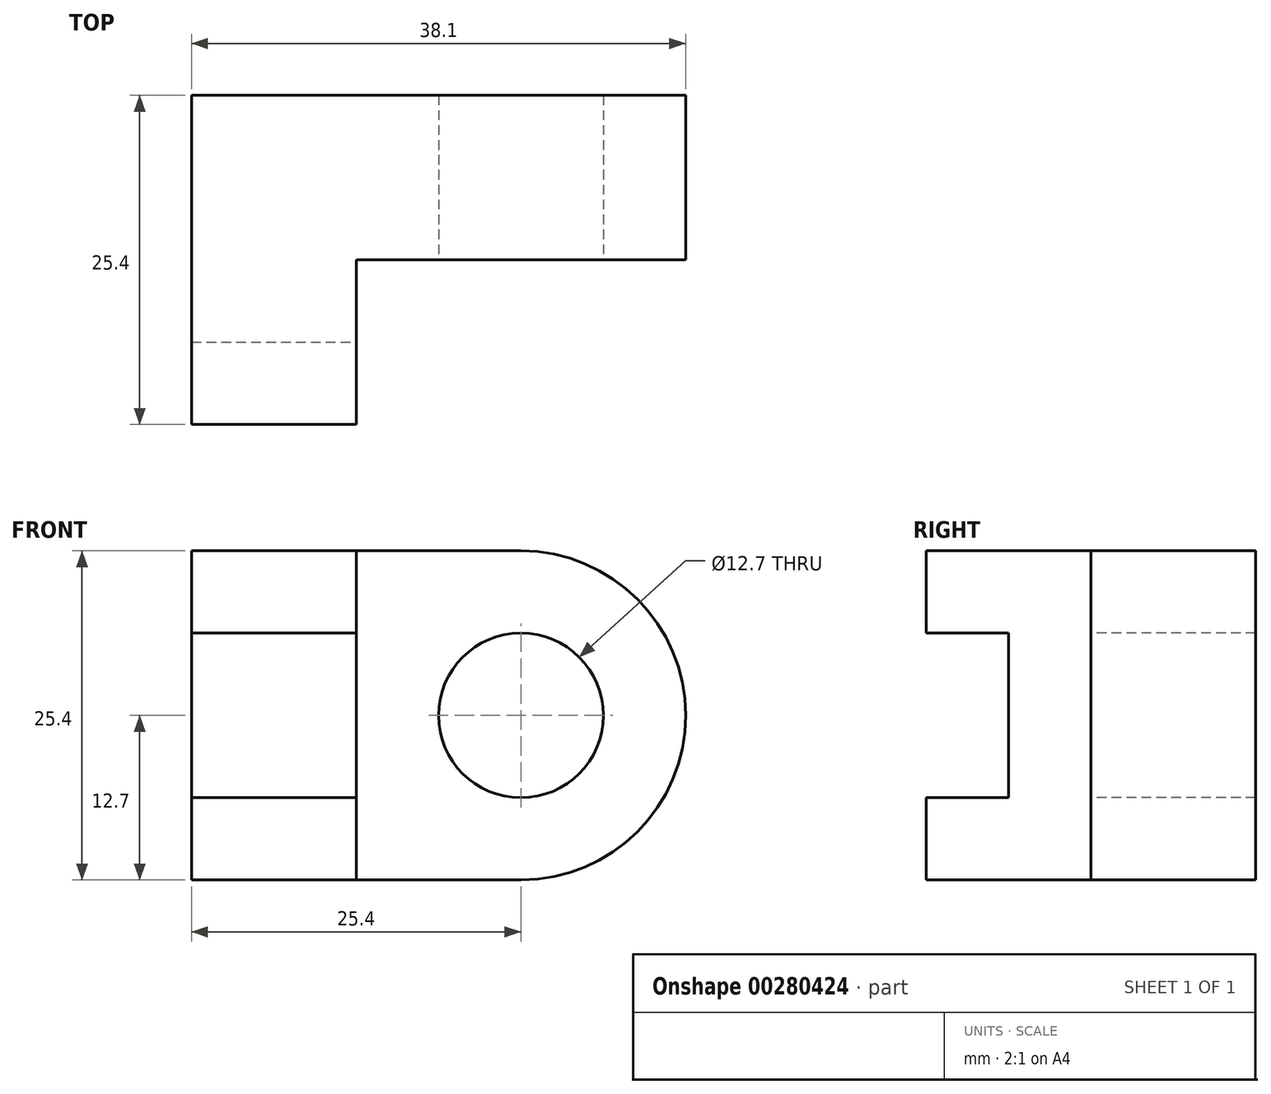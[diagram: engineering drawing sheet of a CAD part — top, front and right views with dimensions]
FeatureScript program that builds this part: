
annotation { "Feature Type Name" : "Feature", "Feature Type Description" : "" }
export const myFeature = defineFeature(function(context is Context, id is Id, definition is map)
    precondition{}
    {
        {
            var Q0;
            Q0=qCreatedBy(makeId("Front.planeOp"),FACE);
            var sketch = newSketch(context, id + "F0", { "sketchPlane" : qUnion([Q0])});
            skLineSegment(sketch, "E0", {"start": v(0, 0) * mm, "end": v(38.1, 0) * mm});
            skLineSegment(sketch, "E1", {"start": v(38.1, 0) * mm, "end": v(38.1, 25.4) * mm});
            skLineSegment(sketch, "E2", {"start": v(38.1, 25.4) * mm, "end": v(0, 25.4) * mm});
            skLineSegment(sketch, "E3", {"start": v(0, 25.4) * mm, "end": v(0, 0) * mm});
            skSolve(sketch);
        }
        {
            var Q0;
            Q0 = qSketchRegion(id + "F0", true);
            extrude(context, id + "F1", {"entities" : qUnion([Q0]), "depth" : 25.4 * mm, "symmetric" : true});
        }
        {
            var Q0;
            Q0=makeQuery(id+"F1.opExtrude","CAP_FACE",FACE,{"disambiguationData":[OSD([sQuery(id+"F0.wireOp",EDGE,"E0"),sQuery(id+"F0.wireOp",EDGE,"E1"),sQuery(id+"F0.wireOp",EDGE,"E2"),sQuery(id+"F0.wireOp",EDGE,"E3")])],"isStart":false});
            var sketch = newSketch(context, id + "F2", { "sketchPlane" : qUnion([Q0])});
            skLineSegment(sketch, "E4", {"start": v(0, 6.35) * mm, "end": v(12.7, 6.35) * mm});
            skLineSegment(sketch, "E5", {"start": v(12.7, 6.35) * mm, "end": v(12.7, 19.05) * mm});
            skLineSegment(sketch, "E6", {"start": v(12.7, 19.05) * mm, "end": v(0, 19.05) * mm});
            skLineSegment(sketch, "E7", {"start": v(0, 19.05) * mm, "end": v(0, 6.35) * mm});
            skSolve(sketch);
        }
        {
            var Q0;
            Q0 = qSketchRegion(id + "F2", true);
            extrude(context, id + "F3", {"entities" : qUnion([Q0]), "operationType" : NewBodyOperationType.REMOVE, "oppositeDirection" : true, "depth" : 6.35 * mm});
        }
        {
            var Q0;
            Q0=makeQuery(id+"F1.opExtrude","SWEPT_FACE",FACE,{"disambiguationData":[OSD([sQuery(id+"F0.wireOp",EDGE,"E2")])]});
            var sketch = newSketch(context, id + "F4", { "sketchPlane" : qUnion([Q0])});
            skLineSegment(sketch, "E8", {"start": v(38.1, -12.7) * mm, "end": v(12.7, -12.7) * mm});
            skLineSegment(sketch, "E9", {"start": v(12.7, -12.7) * mm, "end": v(12.7, 0) * mm});
            skLineSegment(sketch, "E10", {"start": v(12.7, 0) * mm, "end": v(38.1, 0) * mm});
            skLineSegment(sketch, "E11", {"start": v(38.1, 0) * mm, "end": v(38.1, -12.7) * mm});
            skSolve(sketch);
        }
        {
            var Q0;
            Q0 = qSketchRegion(id + "F4", true);
            extrude(context, id + "F5", {"entities" : qUnion([Q0]), "operationType" : NewBodyOperationType.REMOVE, "endBound" : BoundingType.THROUGH_ALL, "oppositeDirection" : true, "depth" : 25.4 * mm});
        }
        {
            var Q0;
            Q0=makeQuery(id+"F5.boolean.opBoolean","COPY",FACE,{"derivedFrom":makeQuery(id+"F5.opExtrude","SWEPT_FACE",FACE,{"disambiguationData":[OSD([sQuery(id+"F4.wireOp",EDGE,"E10")])]})});
            var sketch = newSketch(context, id + "F6", { "sketchPlane" : qUnion([Q0])});
            skLineSegment(sketch, "E12", {"start": v(38.1, 0) * mm, "end": v(25.4, 0) * mm});
            skLineSegment(sketch, "E13", {"start": v(25.4, 0) * mm, "end": v(25.4, 12.7) * mm});
            skLineSegment(sketch, "E14", {"start": v(25.4, 12.7) * mm, "end": v(38.1, 12.7) * mm});
            skLineSegment(sketch, "E15", {"start": v(38.1, 12.7) * mm, "end": v(38.1, 0) * mm});
            skCircle(sketch, "E16", {"center": v(25.4, 12.7) * mm, "radius": 6.35 * mm});
            skSolve(sketch);
        }
        {
            var Q0;
            {var subQ0=sQuery(id+"F6.wireOp",EDGE,"E14");var subQ1=sQuery(id+"F6.wireOp",EDGE,"E13");var subQ2=makeQuery(id+"F6.imprint","INTERSECT",VERTEX,{"derivedFrom":[subQ1,subQ0]});Q0=makeQuery(id+"F6.imprint","IMPRINT",FACE,{"disambiguationData":[TD([[makeQuery(id+"F6.imprint","IMPRINT",EDGE,{"disambiguationData":[TD([[subQ2,1.0]])],"derivedFrom":subQ1}),1.0]])]});}
            var Q1;
            {var subQ0=sQuery(id+"F6.wireOp",EDGE,"E14");var subQ1=sQuery(id+"F6.wireOp",EDGE,"E13");var subQ2=makeQuery(id+"F6.imprint","INTERSECT",VERTEX,{"derivedFrom":[subQ1,subQ0]});Q1=makeQuery(id+"F6.imprint","IMPRINT",FACE,{"disambiguationData":[TD([[makeQuery(id+"F6.imprint","IMPRINT",EDGE,{"disambiguationData":[TD([[subQ2,1.0]])],"derivedFrom":subQ1}),-1.0]])]});}
            extrude(context, id + "F7", {"entities" : qUnion([Q0, Q1]), "operationType" : NewBodyOperationType.REMOVE, "endBound" : BoundingType.THROUGH_ALL, "oppositeDirection" : true, "depth" : 25.4 * mm});
        }
        {
            var Q0;
            Q0=makeQuery(id+"F1.opExtrude","SWEPT_EDGE",EDGE,{"disambiguationData":[OSD([sQuery(id+"F0.wireOp",EDGE,"E1"),sQuery(id+"F0.wireOp",EDGE,"E2")])]});
            fillet(context, id + "F8", {"entities" : qUnion([Q0]), "radius" : 12.7 * mm, "tangentPropagation" : true, "allowEdgeOverflow" : false});
        }
        {
            var Q0;
            Q0=makeQuery(id+"F1.opExtrude","SWEPT_EDGE",EDGE,{"disambiguationData":[OSD([sQuery(id+"F0.wireOp",EDGE,"E0"),sQuery(id+"F0.wireOp",EDGE,"E1")])]});
            fillet(context, id + "F9", {"entities" : qUnion([Q0]), "radius" : 12.7 * mm, "tangentPropagation" : true, "allowEdgeOverflow" : false});
        }
    });
